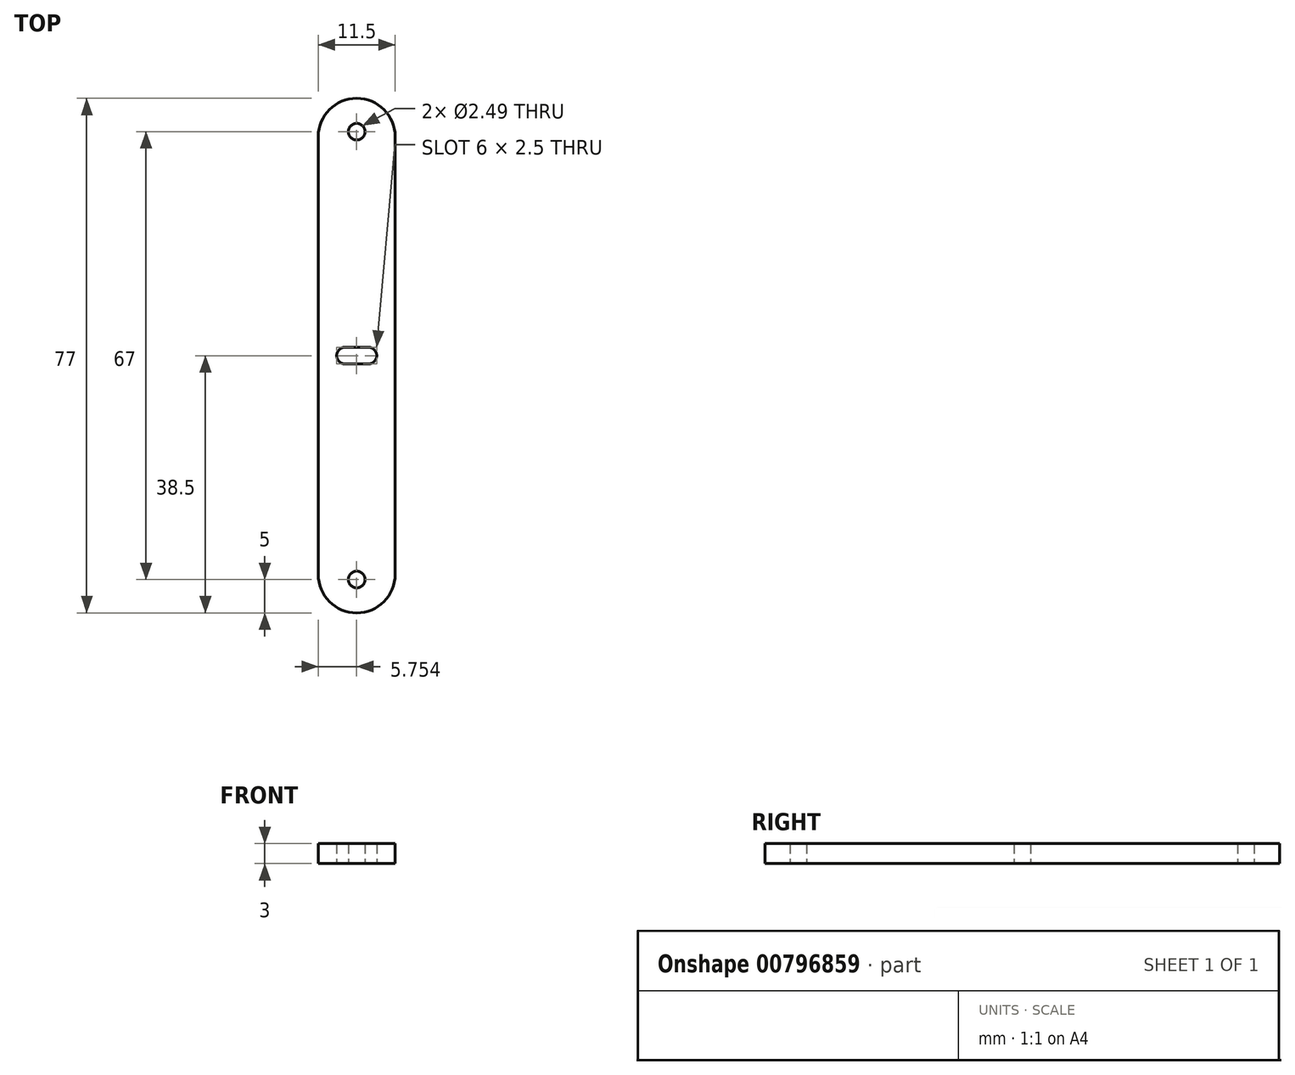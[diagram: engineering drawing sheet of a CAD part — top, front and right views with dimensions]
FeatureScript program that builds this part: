
annotation { "Feature Type Name" : "Feature", "Feature Type Description" : "" }
export const myFeature = defineFeature(function(context is Context, id is Id, definition is map)
    precondition{}
    {
        {
            var Q0;
            Q0=qCreatedBy(makeId("Top.planeOp"),FACE);
            var sketch = newSketch(context, id + "F0", { "sketchPlane" : qUnion([Q0])});
            skLineSegment(sketch, "E0", {"start": v(0, 0) * mm, "end": v(18.75, 0) * mm});
            skLineSegment(sketch, "E1", {"start": v(6.9, -47.95) * mm, "end": v(6.9, 41.47) * mm});
            skLineSegment(sketch, "E2", {"start": v(1.15, 0) * mm, "end": v(1.15, 32.75) * mm});
            skLineSegment(sketch, "E3.MirrorCS", {"start": v(12.65, 0) * mm, "end": v(12.65, 32.75) * mm});
            skLineSegment(sketch, "E4.MirrorCS", {"start": v(1.15, 0) * mm, "end": v(1.15, -32.75) * mm});
            skLineSegment(sketch, "E5.MirrorCS", {"start": v(12.65, 0) * mm, "end": v(12.65, -32.75) * mm});
            skArc(sketch, "E6", {"start": v(12.65, 32.75) * mm, "mid": v(6.9, 38.5) * mm, "end": v(1.15, 32.75) * mm});
            skArc(sketch, "E7.MirrorCS", {"start": v(12.65, -32.75) * mm, "mid": v(6.9, -38.5) * mm, "end": v(1.15, -32.75) * mm});
            skCircle(sketch, "E8", {"center": v(6.9, -33.5) * mm, "radius": 1.25 * mm});
            skCircle(sketch, "E9.MirrorC", {"center": v(6.9, 33.5) * mm, "radius": 1.25 * mm});
            skLineSegment(sketch, "E10", {"start": v(5.15, 1.25) * mm, "end": v(6.9, 1.25) * mm});
            skLineSegment(sketch, "E11.MirrorCS", {"start": v(5.15, -1.25) * mm, "end": v(6.9, -1.25) * mm});
            skArc(sketch, "E12", {"start": v(5.15, 1.25) * mm, "mid": v(3.9, 0) * mm, "end": v(5.15, -1.25) * mm});
            skLineSegment(sketch, "E13.MirrorCS", {"start": v(8.65, 1.25) * mm, "end": v(6.9, 1.25) * mm});
            skLineSegment(sketch, "E14.MirrorCS", {"start": v(8.65, -1.25) * mm, "end": v(6.9, -1.25) * mm});
            skArc(sketch, "E15.MirrorCS", {"start": v(8.65, 1.25) * mm, "mid": v(9.9, 0) * mm, "end": v(8.65, -1.25) * mm});
            skSolve(sketch);
        }
        {
            var Q0;
            Q0 = qSketchRegion(id + "F0", true);
            extrude(context, id + "F1", {"entities" : qUnion([Q0]), "depth" : 3 * mm, "offsetDistance" : 25 * mm});
        }
    });
